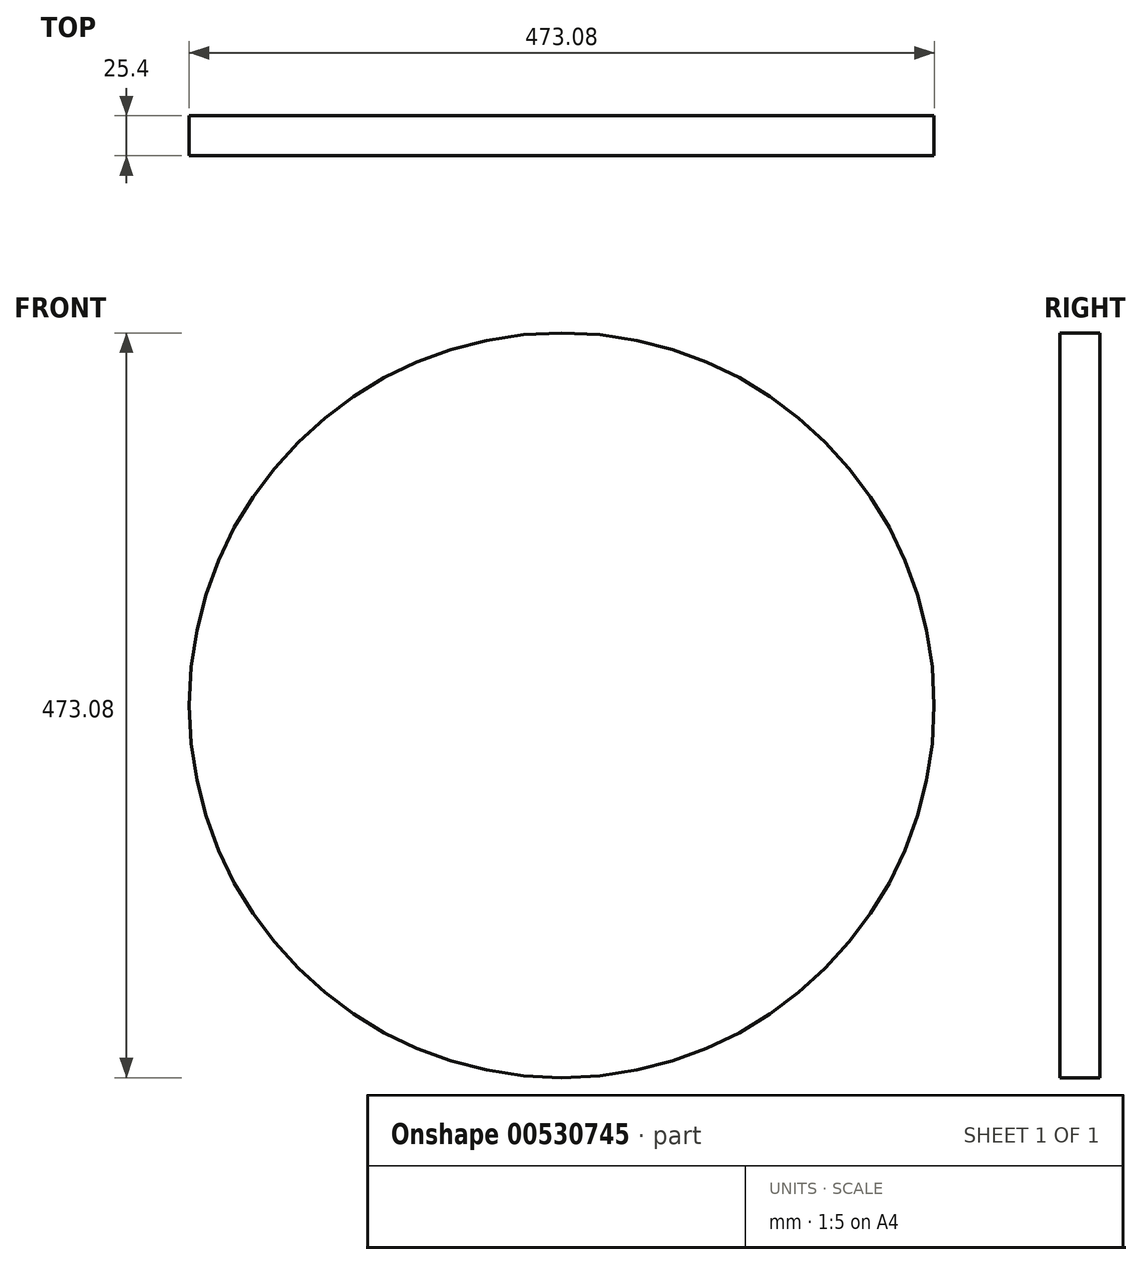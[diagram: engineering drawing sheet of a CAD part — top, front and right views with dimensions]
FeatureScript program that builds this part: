
annotation { "Feature Type Name" : "Feature", "Feature Type Description" : "" }
export const myFeature = defineFeature(function(context is Context, id is Id, definition is map)
    precondition{}
    {
        {
            var Q0;
            Q0=qCreatedBy(makeId("Front.planeOp"),FACE);
            var sketch = newSketch(context, id + "F0", { "sketchPlane" : qUnion([Q0])});
            skCircle(sketch, "E0", {"center": v(0, 0) * mm, "radius": 236.54 * mm});
            skSolve(sketch);
        }
        {
            var Q0;
            Q0=qSketchRegion(id+"F0",true);
            extrude(context, id + "F1", {"entities" : qUnion([Q0]), "depth" : 25.4 * mm});
        }
    });
